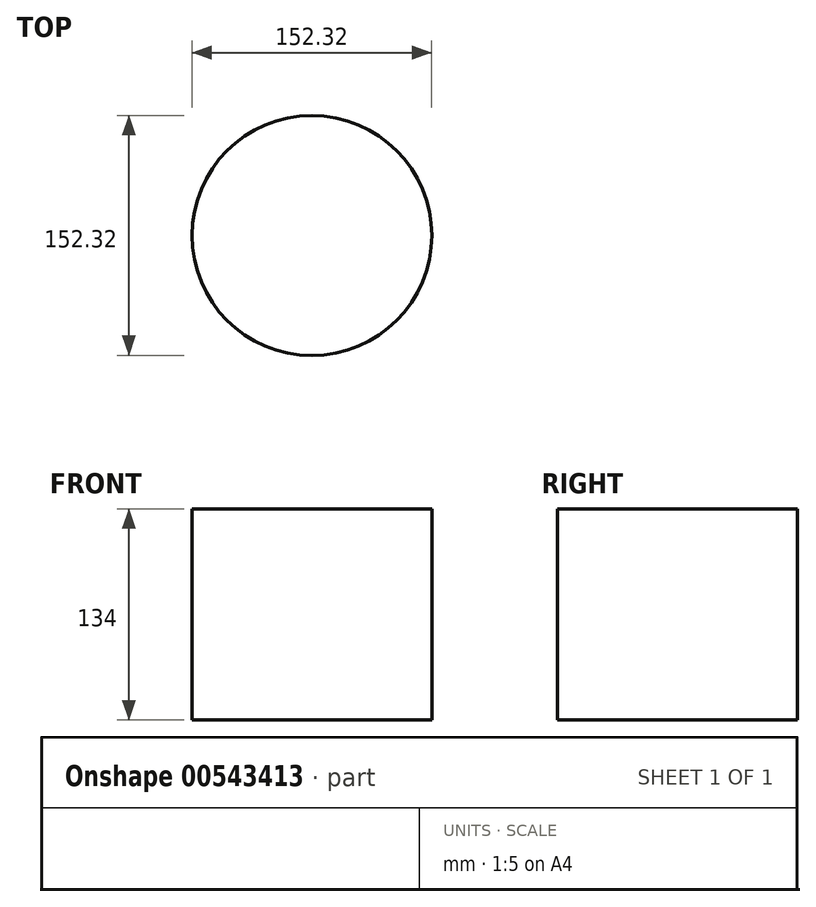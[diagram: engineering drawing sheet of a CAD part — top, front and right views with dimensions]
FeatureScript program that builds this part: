
annotation { "Feature Type Name" : "Feature", "Feature Type Description" : "" }
export const myFeature = defineFeature(function(context is Context, id is Id, definition is map)
    precondition{}
    {
        {
            var Q0;
            Q0=qCreatedBy(makeId("Top.planeOp"),FACE);
            var sketch = newSketch(context, id + "F0", { "sketchPlane" : qUnion([Q0])});
            skCircle(sketch, "E0", {"center": v(0, 0) * mm, "radius": 76.16 * mm});
            skSolve(sketch);
        }
        {
            var Q0;
            Q0=makeQuery(id+"F0.imprint","IMPRINT",FACE,{"disambiguationData":[TD([[makeQuery(id+"F0.imprint","IMPRINT",EDGE,{"derivedFrom":sQuery(id+"F0.wireOp",EDGE,"E0")}),1.0]])]});
            extrude(context, id + "F1", {"entities" : qUnion([Q0]), "endBound" : BoundingType.SYMMETRIC, "depth" : 134 * mm, "offsetDistance" : 25.4 * mm});
        }
    });
